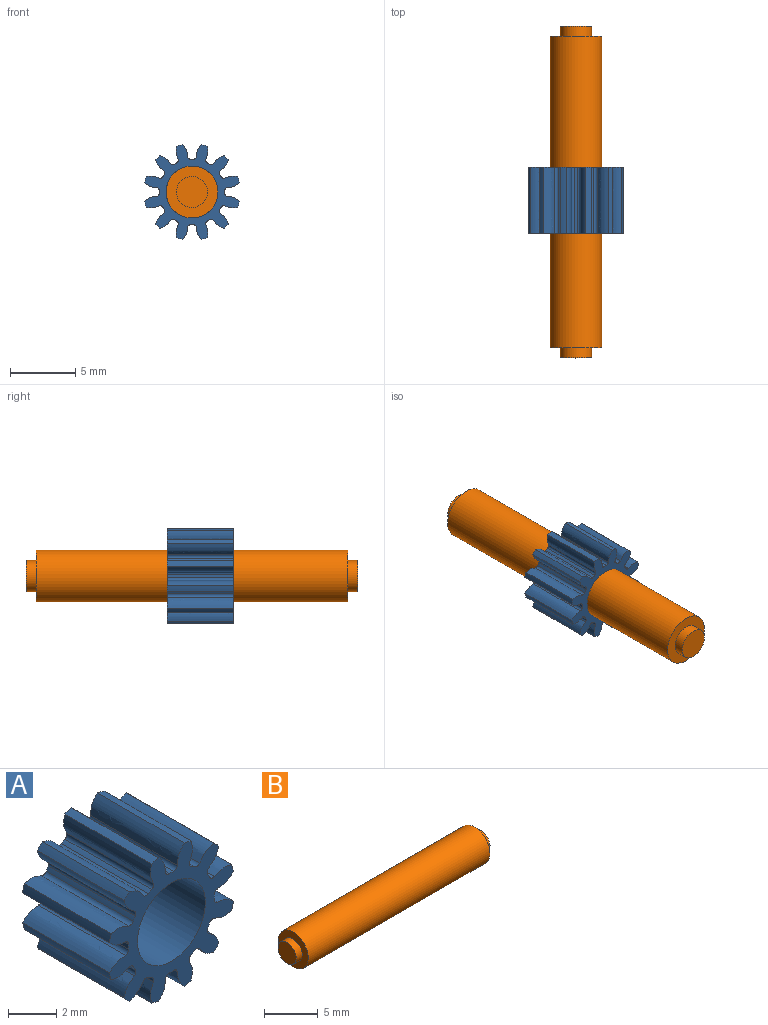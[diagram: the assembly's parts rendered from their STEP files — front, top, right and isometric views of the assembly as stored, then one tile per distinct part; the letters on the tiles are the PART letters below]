
ASSEMBLY  parts=2 mates=1
PART A: 75 faces, bbox 7.3x5.1x7.3 mm
  f0: extruded ~5.08x0.93mm, area 5.4mm2, adj f47,f48,f49,f50
  f1: cylinder r=2.51mm len=5.08mm, axis (0,1,0), area 1.2mm2, adj f48,f49,f50,f51
  f2: extruded ~5.08x0.93mm, area 5.4mm2, adj f3,f48,f49,f51
  f3: cylinder r=3.7mm len=5.08mm, axis (0,1,0), area 2.1mm2, adj f2,f4,f48,f49
  f4: extruded ~5.08x1.01mm, area 5.4mm2, adj f3,f48,f49,f52
  f5: cylinder r=2.51mm len=5.08mm, axis (0,1,0), area 1.2mm2, adj f48,f49,f52,f53
  f6: extruded ~5.08x0.82mm, area 5.4mm2, adj f7,f48,f49,f53
  f7: cylinder r=3.7mm len=5.08mm, axis (0,1,0), area 2.1mm2, adj f6,f8,f48,f49
  f8: extruded ~5.08x0.82mm, area 5.4mm2, adj f7,f48,f49,f54
  f9: cylinder r=2.51mm len=5.08mm, axis (0,1,0), area 1.2mm2, adj f48,f49,f54,f55
  f10: extruded ~5.08x1.01mm, area 5.4mm2, adj f11,f48,f49,f55
  f11: cylinder r=3.7mm len=5.08mm, axis (0,1,0), area 2.1mm2, adj f10,f12,f48,f49
  f12: extruded ~5.08x0.93mm, area 5.4mm2, adj f11,f48,f49,f56
  f13: cylinder r=2.51mm len=5.08mm, axis (0,1,0), area 1.2mm2, adj f48,f49,f56,f57
  f14: extruded ~5.08x0.93mm, area 5.4mm2, adj f15,f48,f49,f57
  f15: cylinder r=3.7mm len=5.08mm, axis (0,1,0), area 2.1mm2, adj f14,f16,f48,f49
  f16: extruded ~5.08x1.01mm, area 5.4mm2, adj f15,f48,f49,f58
  f17: cylinder r=2.51mm len=5.08mm, axis (0,1,0), area 1.2mm2, adj f48,f49,f58,f59
  f18: extruded ~5.08x0.82mm, area 5.4mm2, adj f19,f48,f49,f59
  f19: cylinder r=3.7mm len=5.08mm, axis (0,1,0), area 2.1mm2, adj f18,f20,f48,f49
  f20: extruded ~5.08x0.82mm, area 5.4mm2, adj f19,f48,f49,f60
  f21: cylinder r=2.51mm len=5.08mm, axis (0,1,0), area 1.2mm2, adj f48,f49,f60,f61
  f22: extruded ~5.08x1.01mm, area 5.4mm2, adj f23,f48,f49,f61
  f23: cylinder r=3.7mm len=5.08mm, axis (0,1,0), area 2.1mm2, adj f22,f24,f48,f49
  f24: extruded ~5.08x0.93mm, area 5.4mm2, adj f23,f48,f49,f62
  f25: cylinder r=2.51mm len=5.08mm, axis (0,1,0), area 1.2mm2, adj f48,f49,f62,f63
  f26: extruded ~5.08x0.93mm, area 5.4mm2, adj f27,f48,f49,f63
  f27: cylinder r=3.7mm len=5.08mm, axis (0,1,0), area 2.1mm2, adj f26,f28,f48,f49
  f28: extruded ~5.08x1.01mm, area 5.4mm2, adj f27,f48,f49,f64
  f29: cylinder r=2.51mm len=5.08mm, axis (0,1,0), area 1.2mm2, adj f48,f49,f64,f65
  f30: extruded ~5.08x0.82mm, area 5.4mm2, adj f31,f48,f49,f65
  f31: cylinder r=3.7mm len=5.08mm, axis (0,1,0), area 2.1mm2, adj f30,f32,f48,f49
  f32: extruded ~5.08x0.82mm, area 5.4mm2, adj f31,f48,f49,f66
  f33: cylinder r=2.51mm len=5.08mm, axis (0,1,0), area 1.2mm2, adj f48,f49,f66,f67
  f34: extruded ~5.08x1.01mm, area 5.4mm2, adj f35,f48,f49,f67
  f35: cylinder r=3.7mm len=5.08mm, axis (0,1,0), area 2.1mm2, adj f34,f36,f48,f49
  f36: extruded ~5.08x0.93mm, area 5.4mm2, adj f35,f48,f49,f68
  f37: cylinder r=2.51mm len=5.08mm, axis (0,1,0), area 1.2mm2, adj f48,f49,f68,f69
  f38: extruded ~5.08x0.93mm, area 5.4mm2, adj f39,f48,f49,f69
  f39: cylinder r=3.7mm len=5.08mm, axis (0,1,0), area 2.1mm2, adj f38,f40,f48,f49
  f40: extruded ~5.08x1.01mm, area 5.4mm2, adj f39,f48,f49,f70
  f41: cylinder r=2.51mm len=5.08mm, axis (0,1,0), area 1.2mm2, adj f48,f49,f70,f71
  f42: extruded ~5.08x0.82mm, area 5.4mm2, adj f43,f48,f49,f71
  f43: cylinder r=3.7mm len=5.08mm, axis (0,1,0), area 2.1mm2, adj f42,f44,f48,f49
  f44: extruded ~5.08x0.82mm, area 5.4mm2, adj f43,f48,f49,f72
  f45: cylinder r=2.51mm len=5.08mm, axis (0,1,0), area 1.2mm2, adj f48,f49,f72,f73
  f46: extruded ~5.08x1.01mm, area 5.4mm2, adj f47,f48,f49,f73
  f47: cylinder r=3.7mm len=5.08mm, axis (0,1,0), area 2.1mm2, adj f0,f46,f48,f49
  f48: plane 7.28x7.28mm, normal (0,-1,0), area 18.1mm2, adj f0,f1,f2,f3,f4,f5,f6,f7
  f49: plane 7.28x7.28mm, normal (0,1,0), area 18.1mm2, adj f0,f1,f2,f3,f4,f5,f6,f7
  f50: cylinder r=0.21mm len=5.08mm, axis (0,1,0), area 1.6mm2, adj f0,f1,f48,f49
  f51: cylinder r=0.21mm len=5.08mm, axis (0,1,0), area 1.6mm2, adj f1,f2,f48,f49
  f52: cylinder r=0.21mm len=5.08mm, axis (0,1,0), area 1.6mm2, adj f4,f5,f48,f49
  f53: cylinder r=0.21mm len=5.08mm, axis (0,1,0), area 1.6mm2, adj f5,f6,f48,f49
  f54: cylinder r=0.21mm len=5.08mm, axis (0,1,0), area 1.6mm2, adj f8,f9,f48,f49
  f55: cylinder r=0.21mm len=5.08mm, axis (0,1,0), area 1.6mm2, adj f9,f10,f48,f49
  f56: cylinder r=0.21mm len=5.08mm, axis (0,1,0), area 1.6mm2, adj f12,f13,f48,f49
  f57: cylinder r=0.21mm len=5.08mm, axis (0,1,0), area 1.6mm2, adj f13,f14,f48,f49
  f58: cylinder r=0.21mm len=5.08mm, axis (0,1,0), area 1.6mm2, adj f16,f17,f48,f49
  f59: cylinder r=0.21mm len=5.08mm, axis (0,1,0), area 1.6mm2, adj f17,f18,f48,f49
  f60: cylinder r=0.21mm len=5.08mm, axis (0,1,0), area 1.6mm2, adj f20,f21,f48,f49
  f61: cylinder r=0.21mm len=5.08mm, axis (0,1,0), area 1.6mm2, adj f21,f22,f48,f49
  f62: cylinder r=0.21mm len=5.08mm, axis (0,1,0), area 1.6mm2, adj f24,f25,f48,f49
  f63: cylinder r=0.21mm len=5.08mm, axis (0,1,0), area 1.6mm2, adj f25,f26,f48,f49
  f64: cylinder r=0.21mm len=5.08mm, axis (0,1,0), area 1.6mm2, adj f28,f29,f48,f49
  f65: cylinder r=0.21mm len=5.08mm, axis (0,1,0), area 1.6mm2, adj f29,f30,f48,f49
  f66: cylinder r=0.21mm len=5.08mm, axis (0,1,0), area 1.6mm2, adj f32,f33,f48,f49
  f67: cylinder r=0.21mm len=5.08mm, axis (0,1,0), area 1.6mm2, adj f33,f34,f48,f49
  f68: cylinder r=0.21mm len=5.08mm, axis (0,1,0), area 1.6mm2, adj f36,f37,f48,f49
  f69: cylinder r=0.21mm len=5.08mm, axis (0,1,0), area 1.6mm2, adj f37,f38,f48,f49
  f70: cylinder r=0.21mm len=5.08mm, axis (0,1,0), area 1.6mm2, adj f40,f41,f48,f49
  f71: cylinder r=0.21mm len=5.08mm, axis (0,1,0), area 1.6mm2, adj f41,f42,f48,f49
  f72: cylinder r=0.21mm len=5.08mm, axis (0,1,0), area 1.6mm2, adj f44,f45,f48,f49
  f73: cylinder r=0.21mm len=5.08mm, axis (0,1,0), area 1.6mm2, adj f45,f46,f48,f49
  f74: cylinder r=1.98mm len=5.08mm, axis (0,1,0), area 63.3mm2, adj f48,f49
PART B: 7 faces, bbox 25.4x4x4 mm
  f0: cylinder r=1.19mm len=2.38mm, axis (-1,0,0), area 5.9mm2, adj f1,f3
  f1: plane 2.38x2.38mm, normal (1,0,0), area 4.5mm2, adj f0
  f2: cylinder r=1.98mm len=23.81mm, axis (-1,0,0), area 296.9mm2, adj f3,f4
  f3: plane 3.97x3.97mm, normal (1,0,0), area 7.9mm2, adj f0,f2
  f4: plane 3.97x3.97mm, normal (-1,0,0), area 7.9mm2, adj f2,f6
  f5: plane 2.38x2.38mm, normal (-1,0,0), area 4.5mm2, adj f6
  f6: cylinder r=1.19mm len=2.38mm, axis (-1,0,0), area 5.9mm2, adj f4,f5
PLACE A t=(-10.58,1.62,-1.98)mm
PLACE B rot(axis=(0.58,-0.58,-0.58),120deg) t=(-10.58,12.42,-1.98)mm
MATE fastened A.f74 <-> B.f0  axis (0,1,0) through (-10.58,-3.46,-1.98)mm
